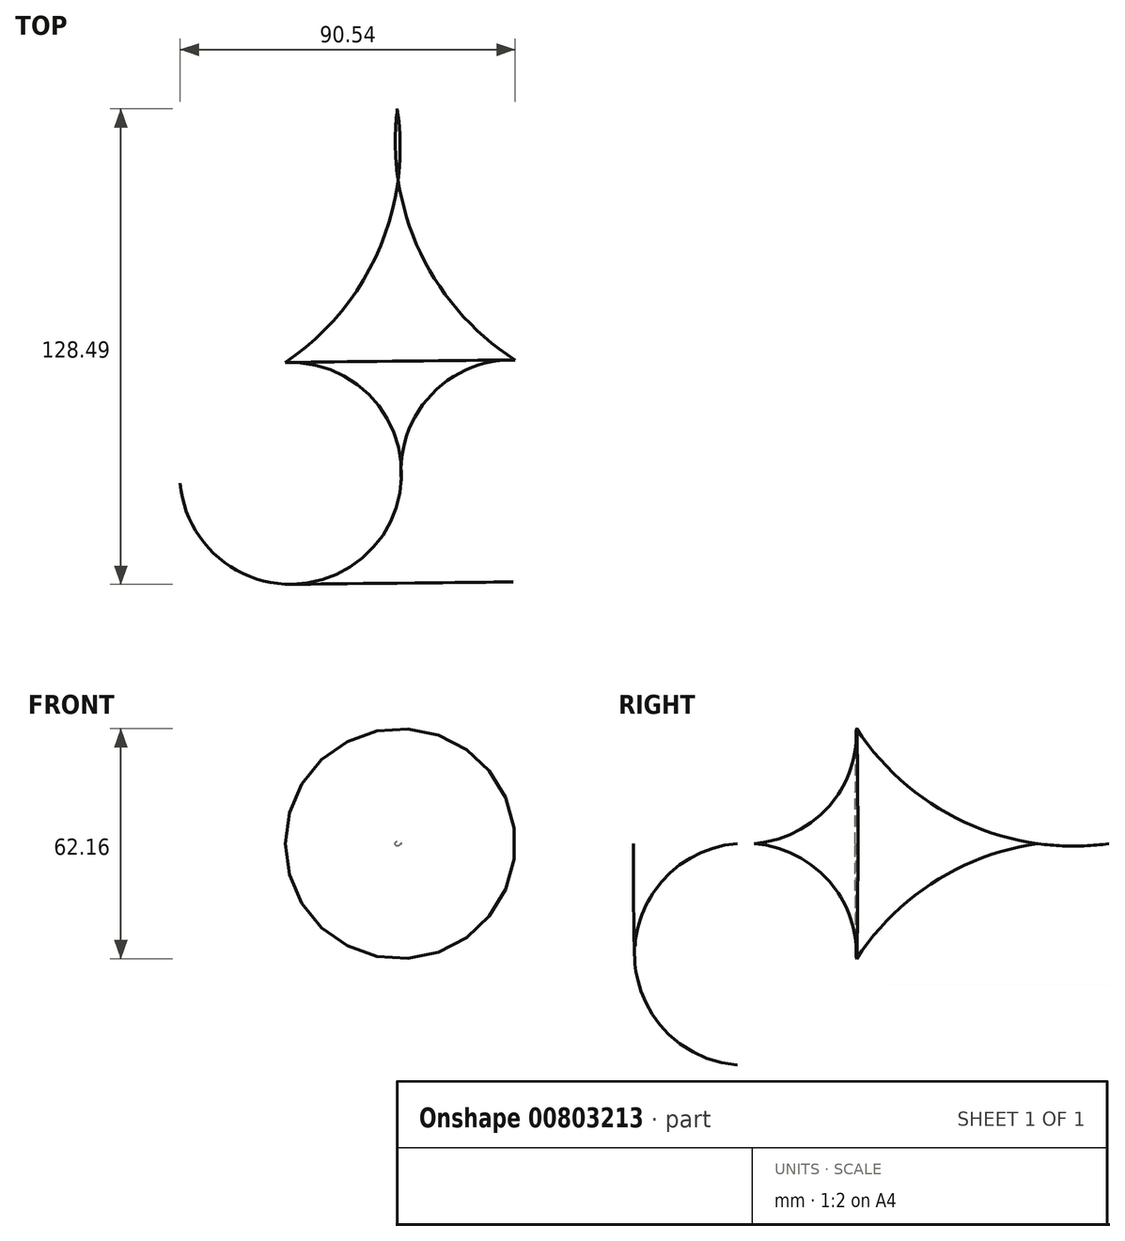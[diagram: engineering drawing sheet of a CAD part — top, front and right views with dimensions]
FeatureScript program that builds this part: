
annotation { "Feature Type Name" : "Feature", "Feature Type Description" : "" }
export const myFeature = defineFeature(function(context is Context, id is Id, definition is map)
    precondition{}
    {
        {
            var Q0;
            Q0=qCreatedBy(makeId("Top.planeOp"),FACE);
            var sketch = newSketch(context, id + "F0", { "sketchPlane" : qUnion([Q0])});
            skLineSegment(sketch, "E0", {"start": v(-1.63, 84.37) * mm, "end": v(0.26, -85.96) * mm, "construction": true});
            skArc(sketch, "E1", {"start": v(30.4, 0) * mm, "mid": v(7.7, -9.43) * mm, "end": v(-0.33, -32.65) * mm});
            skArc(sketch, "E2", {"start": v(-1.23, 48.7) * mm, "mid": v(9.3, 20.92) * mm, "end": v(30.4, 0) * mm});
            skLineSegment(sketch, "E3", {"start": v(-0.33, -32.65) * mm, "end": v(-1.23, 48.7) * mm});
            skSolve(sketch);
        }
        {
            var Q0;
            {var subQ0=sQuery(id+"F0.wireOp",EDGE,"E2");Q0=makeQuery(id+"F0.imprint","IMPRINT",FACE,{"disambiguationData":[TD([[makeQuery(id+"F0.imprint","IMPRINT",EDGE,{"derivedFrom":subQ0}),-1.0]])]});}
            var Q1;
            Q1=sQuery(id+"F0.wireOp",EDGE,"E0");
            revolve(context, id + "F1", {"surfaceOperationType" : NewSurfaceOperationType.NEW, "entities" : qUnion([Q0]), "axis" : qUnion([Q1]), "revolveType" : RevolveType.FULL});
        }
    });
